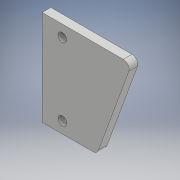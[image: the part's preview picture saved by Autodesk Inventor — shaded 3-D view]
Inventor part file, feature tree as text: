
AUTODESK INVENTOR PART (.ipt)
format: ipt  version: 2017 (Build 210142000, 142)  size: 114,176 bytes
history: native  units: mm
features: fillet x2, sketch x2, extrude x1, hole x1
ambient origin geometry x8: Origin, YZ Plane, XZ Plane, XY Plane, X Axis, Y Axis, Z Axis, Center Point
bodies: Solid1 (feature_tree)
feature tree (6):
  extrude  "Extrusion1"  Depth=33.0mm
  hole  "Hole1"  [1 undecoded]
  fillet  "Fillet1"  Radius=4.0mm
  fillet  "Fillet2"  Radius=7.0mm
  sketch  "Sketch1"  dims[d1=33.0mm d2=3.490659mm]
  sketch  "Sketch3"  dims[d3=3.0mm d4=0.0mm d5=4.0mm d6=4.0mm d9=3.0mm d10=6.0mm d11=4.0mm d12=2.0mm d13=90.0deg d14=8.0mm d15=20.594885mm d19=7.0mm d21=7.0mm d22=19.0mm d23=2.0mm d24=2.0mm]
note: 1 required parameter value undecoded (feature->parameter linkage not recoverable at this tier; creation-order binding heuristic only, values carry confidence <= 0.55)
